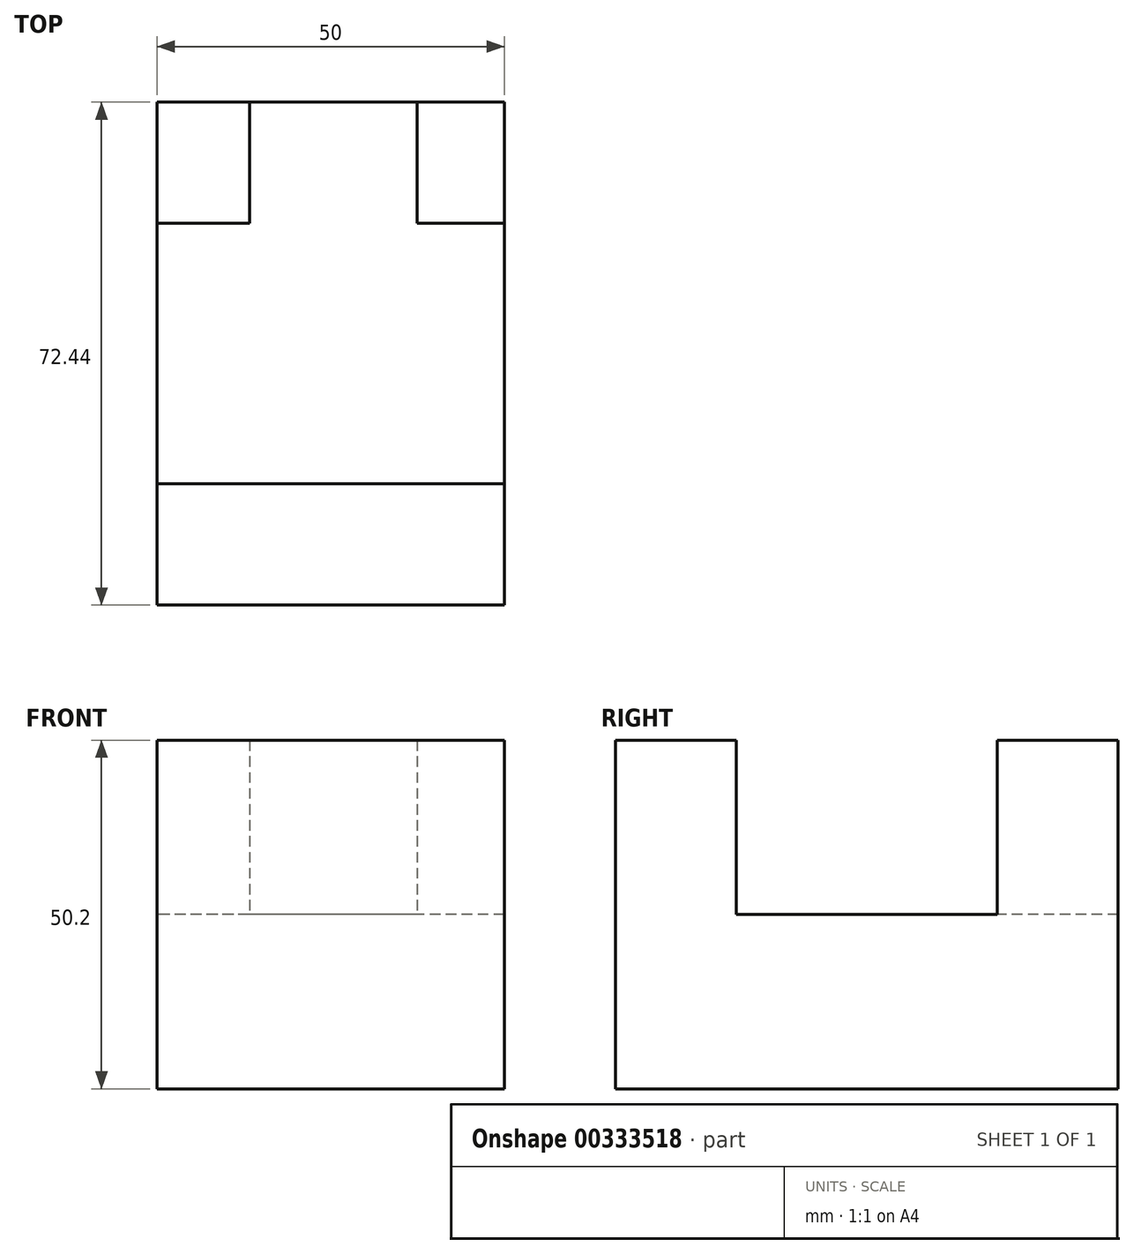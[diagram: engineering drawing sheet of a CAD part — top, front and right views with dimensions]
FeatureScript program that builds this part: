
annotation { "Feature Type Name" : "Feature", "Feature Type Description" : "" }
export const myFeature = defineFeature(function(context is Context, id is Id, definition is map)
    precondition{}
    {
        {
            var Q0;
            Q0=qCreatedBy(makeId("Right.planeOp"),FACE);
            var sketch = newSketch(context, id + "F0", { "sketchPlane" : qUnion([Q0])});
            skLineSegment(sketch, "E0.bottom", {"start": v(-36.22, 25.1) * mm, "end": v(-18.79, 25.1) * mm});
            skLineSegment(sketch, "E0.top", {"start": v(-36.22, -25.1) * mm, "end": v(36.22, -25.1) * mm});
            skLineSegment(sketch, "E0.left", {"start": v(-36.22, 25.1) * mm, "end": v(-36.22, -25.1) * mm});
            skLineSegment(sketch, "E0.right", {"start": v(36.22, 25.1) * mm, "end": v(36.22, -25.1) * mm});
            skPoint(sketch, "E0.middle", {"position": v(0, 0) * mm});
            skLineSegment(sketch, "E1.top", {"start": v(-18.79, 0) * mm, "end": v(18.79, 0) * mm});
            skLineSegment(sketch, "E1.left", {"start": v(-18.79, 25.1) * mm, "end": v(-18.79, 0) * mm});
            skLineSegment(sketch, "E1.right", {"start": v(18.79, 25.1) * mm, "end": v(18.79, 0) * mm});
            skLineSegment(sketch, "E2.trimOffspring", {"start": v(18.79, 25.1) * mm, "end": v(36.22, 25.1) * mm});
            skSolve(sketch);
        }
        {
            var Q0;
            Q0=makeQuery(id+"F0.imprint","IMPRINT",FACE,{"disambiguationData":[TD([[makeQuery(id+"F0.imprint","IMPRINT",EDGE,{"derivedFrom":sQuery(id+"F0.wireOp",EDGE,"E0.bottom")}),-1.0]])]});
            extrude(context, id + "F1", {"entities" : qUnion([Q0]), "depth" : 50 * mm, "offsetDistance" : 25 * mm});
        }
        {
            var Q0;
            Q0=qCreatedBy(makeId("Front.planeOp"),FACE);
            var sketch = newSketch(context, id + "F2", { "sketchPlane" : qUnion([Q0])});
            skLineSegment(sketch, "E3.bottom", {"start": v(13.34, 0) * mm, "end": v(37.47, 0) * mm});
            skLineSegment(sketch, "E3.top", {"start": v(13.34, 28.32) * mm, "end": v(37.47, 28.32) * mm});
            skLineSegment(sketch, "E3.left", {"start": v(13.34, 0) * mm, "end": v(13.34, 28.32) * mm});
            skLineSegment(sketch, "E3.right", {"start": v(37.47, 0) * mm, "end": v(37.47, 28.32) * mm});
            skSolve(sketch);
        }
        {
            var Q0;
            Q0=makeQuery(id+"F2.imprint","IMPRINT",FACE,{"disambiguationData":[TD([[makeQuery(id+"F2.imprint","IMPRINT",EDGE,{"derivedFrom":sQuery(id+"F2.wireOp",EDGE,"E3.bottom")}),1.0]])]});
            extrude(context, id + "F3", {"entities" : qUnion([Q0]), "operationType" : NewBodyOperationType.REMOVE, "oppositeDirection" : true, "depth" : 100 * mm, "offsetDistance" : 25 * mm});
        }
    });
